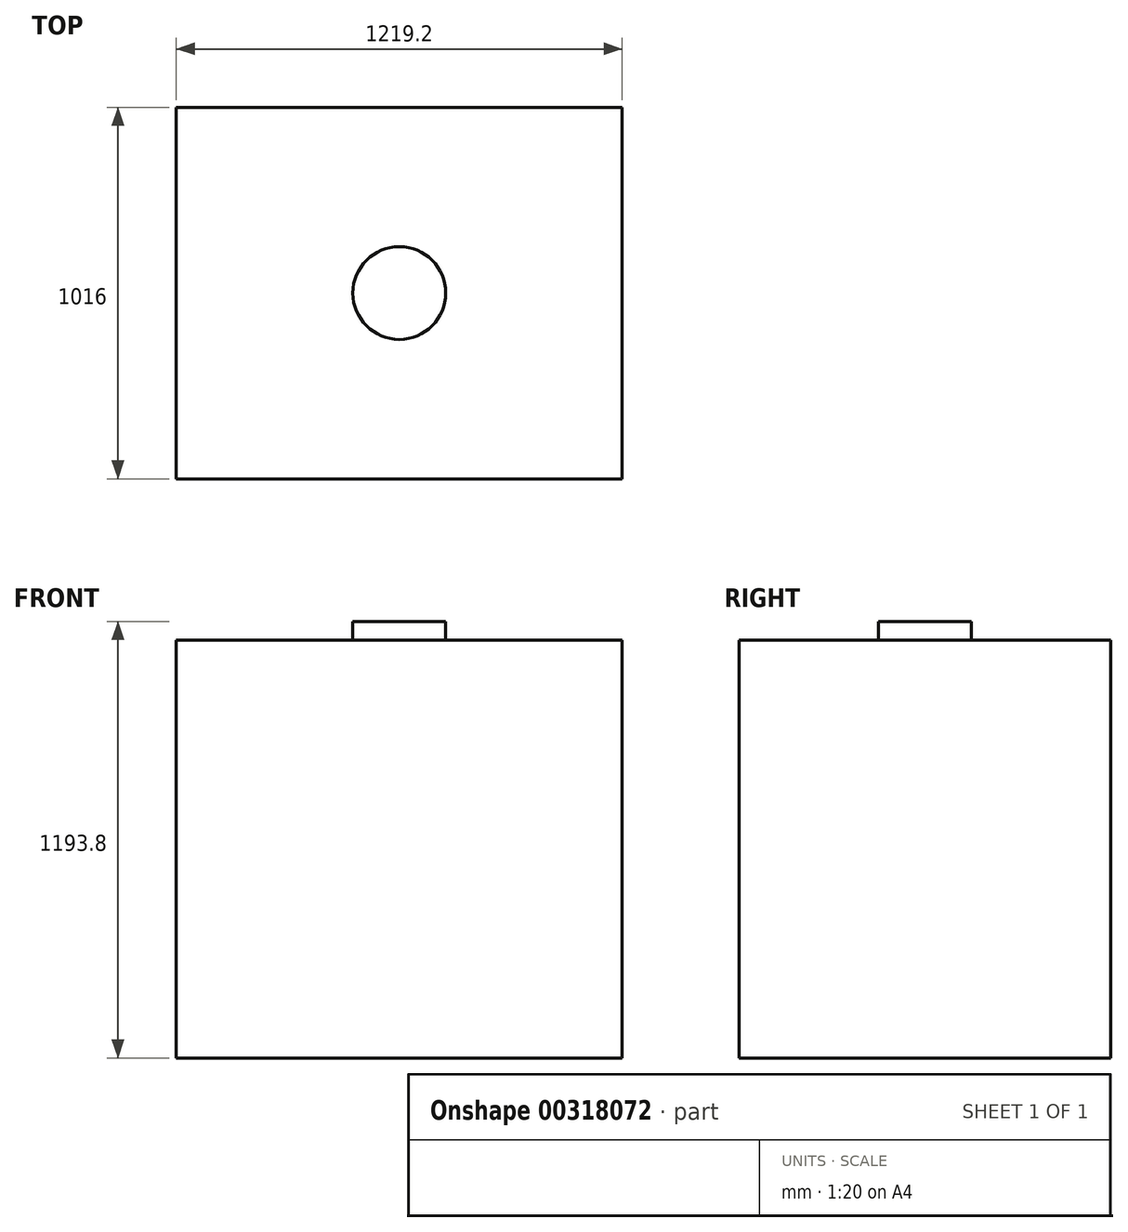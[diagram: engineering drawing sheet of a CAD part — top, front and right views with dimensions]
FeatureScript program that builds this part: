
annotation { "Feature Type Name" : "Feature", "Feature Type Description" : "" }
export const myFeature = defineFeature(function(context is Context, id is Id, definition is map)
    precondition{}
    {
        {
            var Q0;
            Q0=qCreatedBy(makeId("Front.planeOp"),FACE);
            var sketch = newSketch(context, id + "F0", { "sketchPlane" : qUnion([Q0])});
            skLineSegment(sketch, "E0.bottom", {"start": v(-1219.2, 1143) * mm, "end": v(0, 1143) * mm});
            skLineSegment(sketch, "E0.top", {"start": v(-1219.2, 0) * mm, "end": v(0, 0) * mm});
            skLineSegment(sketch, "E0.left", {"start": v(-1219.2, 1143) * mm, "end": v(-1219.2, 0) * mm});
            skLineSegment(sketch, "E0.right", {"start": v(0, 1143) * mm, "end": v(0, 0) * mm});
            skSolve(sketch);
        }
        {
            var Q0;
            Q0=qSketchRegion(id+"F0",true);
            extrude(context, id + "F1", {"entities" : qUnion([Q0]), "depth" : 1016 * mm, "offsetDistance" : 25.4 * mm});
        }
        {
            var Q0;
            Q0=makeQuery(id+"F1.opExtrude","SWEPT_FACE",FACE,{"disambiguationData":[OSD([sQuery(id+"F0.wireOp",EDGE,"E0.bottom")])]});
            var sketch = newSketch(context, id + "F2", { "sketchPlane" : qUnion([Q0])});
            skCircle(sketch, "E1", {"center": v(-609.6, -508) * mm, "radius": 127 * mm});
            skLineSegment(sketch, "E2", {"start": v(-1219.2, -1016) * mm, "end": v(0, 0) * mm, "construction": true});
            skSolve(sketch);
        }
        {
            var Q0;
            Q0=makeQuery(id+"F2.imprint","IMPRINT",FACE,{"disambiguationData":[TD([[makeQuery(id+"F2.imprint","IMPRINT",EDGE,{"derivedFrom":sQuery(id+"F2.wireOp",EDGE,"E1")}),1.0]])]});
            extrude(context, id + "F3", {"entities" : qUnion([Q0]), "operationType" : NewBodyOperationType.ADD, "depth" : 50.8 * mm, "offsetDistance" : 25.4 * mm});
        }
    });
